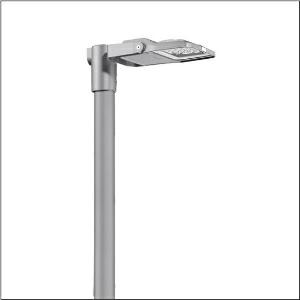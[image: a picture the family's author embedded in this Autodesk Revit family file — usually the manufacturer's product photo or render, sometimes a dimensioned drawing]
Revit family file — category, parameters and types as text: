
# Revit family: floodlight_fl_21_iq_micro___pl52_5xa7761a4d3a_5d98
name_source: partatom
category: Lighting Fixtures
units: mm (PartAtom-declared; Revit-internal decimal feet)

## family parameters
Cut with Voids When Loaded = No
Host = Face
Light Source = No
Part Type = Normal
Room Calculation Point = No
Round Connector Dimension = Use Diameter
Shared = No

## types (1)
- --- (1 x LED, 3010 lm, 23.1 W, 4000K)
    Apparent Load = 23 VA
    CIE Flux Codes = 26 60 98 100 100
    Color Rendering = 70
    Color Temperature = 4000K
    Default Elevation = 1800 mm
    Description = Floodlight FL 21 iQ micro, floodlight, primary light control with lens, of PMMA, primary optical cover: protective disc, of toughened safety glass, transparent, light distribution: PL52, light emission: direct distribution, installation type: surface-mounted, LED, High Power LED, rated luminous flux: 3.010lm, luminous efficacy: 130lm/W, light colour: 740, colour temperature: 4000K, control: optimised constant luminous flux control (CLO 2.0), Desk-Remote (wireless, voltage-free reading and setting of iQ features in the workshop via application-optimized NFC function/RFID function), Light-Fading, Smart-Wire, Night-Set, Lumen-Switch, Temp-Guard, Auto-Match, with terminal, 6-pole, mains connection: 220..240V, AC, 50/60Hz, start of lifetime: 23W, end of service life: 24W, reduction: 11W, luminaire housing, of diecast aluminium, powder-coated, Siteco® metallic grey (DB 702S), corrosivity category C5 mid according to DIN EN ISO 12944, sealing non-destructively replaceable, please order mast flange separately, mast bracket, of steel, galvanised, powder-coated, Siteco® metallic grey (DB 702S), protection rating (complete): IP66, insulation class (complete): insulation class II (safety insulation), certification: CE, ENEC, VDE, protection symbol: D, impact resistance: IK07, permissible operating ambient temperature: -40..+40°C, permissible operating ambient temperature for outdoor applications: -40..+50°C, standard: DIN EN 12944, LABS conformity tested according to VDMA 24364:2018-05, packaging unit: 1 piece

Light Distribution: PL52
    Height = 65 mm
    Lamp = 1 x LED
    Lamp Light Flux = 3010 lm
    Lamp Power = 23.1 W
    Lamp count = 1
    Length = 312 mm
    Luminous efficacy = 130 lm/W
    Manufacturer = Siteco
    ModVariant = No
    Model = 5XA7761A4D3A
    Number of Poles = 1
    OnlyDefault = Yes
    Power Factor = 1
    Product Name = Floodlight FL 21 iQ micro | PL52
    Product group = floodlight | pylon annexe
    ProductGroupID = 6200
    Protection Class = Protection class II
    Protection Degree = IP 66
    RLX_Detail_Level = 1
    RLX_Emergency_Light_Flux = 0 lm
    RLX_Emergency_Type = 0
    RLX_Emergency_Type_DB = No
    RlxData = <blob elided: 102057 chars, md5=c3ba4e2f>
    Socket = socket
    Standby Power = 0 W
    System Light Flux = 3010 lm
    System Power = 23 W
    Type Comments = factory setting: luminous flux: 100 % | dim-lin: 254 | 455 mA
    Type Image = l_1007121.jpg
    URL = http://relux.com
    VarID = @adj_149275
    Voltage = 0 V
    Weight = 0.00 kg
    Width = 230 mm

## geometry (parser evidence)
native form markers: Blend x4, Sweep x13
no freeform markers — native parametric forms only
